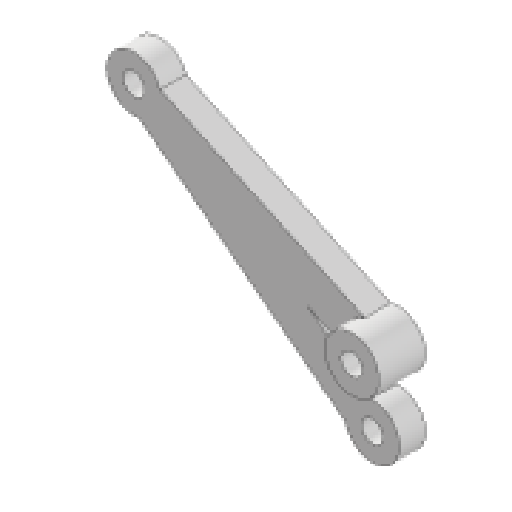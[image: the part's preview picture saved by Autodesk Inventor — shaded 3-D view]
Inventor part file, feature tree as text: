
AUTODESK INVENTOR PART (.ipt)
format: ipt  version: 2025 (Build 290162010, 162A)  size: 130,560 bytes
history: native  units: in
note: dims shown in document units (in); Inventor stores cm internally (conversion verified against a paired STEP export)
features: extrude x2, sketch x2
ambient origin geometry x8: Origin, YZ Plane, XZ Plane, XY Plane, X Axis, Y Axis, Z Axis, Center Point
bodies: Solid1 (feature_tree)
feature tree (4):
  extrude  "Extrusion1"  Depth=0.16in
  extrude  "Extrusion4"  Depth=0.15in
  sketch  "Sketch1"  dims[d0=0.4in d1=0.16in]
  sketch  "Sketch4"  dims[d7=0.4in d8=0.16in d9=0.5in d10=0.3in d11=0.15in d12=60.0deg d14=0.19in d15=0.0in d20=0.4in d21=0.16in d25=0.3in d29=1.75in d30=0.3in d31=0.15in d32=1.0in d33=0.1718in d34=0.15in d35=0.0in]
